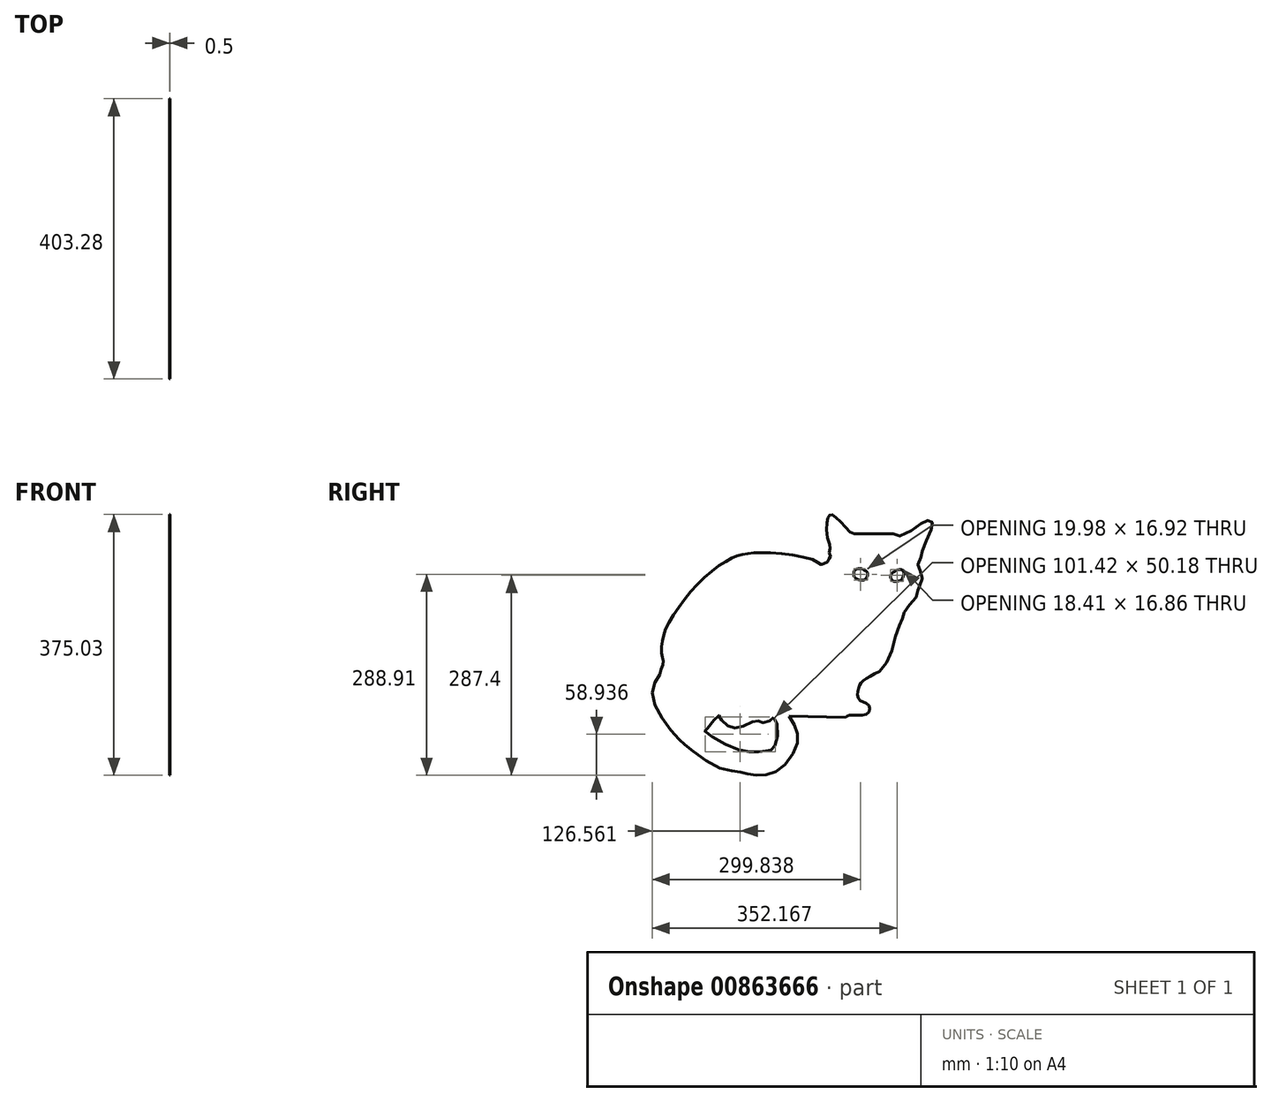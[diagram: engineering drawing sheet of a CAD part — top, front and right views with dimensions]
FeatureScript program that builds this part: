
annotation { "Feature Type Name" : "Feature", "Feature Type Description" : "" }
export const myFeature = defineFeature(function(context is Context, id is Id, definition is map)
    precondition{}
    {
        {
            var Q0;
            Q0=qCreatedBy(makeId("Right.planeOp"),FACE);
            var sketch = newSketch(context, id + "F0", { "sketchPlane" : qUnion([Q0])});
            skLineSegment(sketch, "E0", {"start": v(28.7, 28.02) * mm, "end": v(17.6, 28.02) * mm});
            skLineSegment(sketch, "E1", {"start": v(-11.4, 22.53) * mm, "end": v(-6.57, 22.53) * mm});
            skFitSpline(sketch, "E2", {"points": [v(17.6, 28.02) * mm, v(16.08, 28.8) * mm, v(13.76, 31.39) * mm, v(11.74, 33.19) * mm, v(11.02, 33.6) * mm, v(10.4, 33.43) * mm, v(9.92, 32.72) * mm, v(9.66, 31.07) * mm, v(9.8, 27.16) * mm, v(10.6, 24.27) * mm, v(10.44, 23.51) * mm, v(10.44, 22.03) * mm, v(10.73, 21.57) * mm, v(10.35, 21.16) * mm, v(10.15, 20.23) * mm, v(7.73, 19.24) * mm, v(6.81, 20.06) * mm, v(2, 21.54) * mm, v(-6.57, 22.53) * mm], "startDerivative": vector(-30.35, 0) * mm, "endDerivative": vector(-74.71, 0) * mm});
            skFitSpline(sketch, "E3", {"points": [v(-11.4, 22.53) * mm, v(-15.14, 21.98) * mm, v(-18.68, 20.56) * mm, v(-25.5, 15.58) * mm, v(-32.77, 7.2) * mm, v(-36.9, 0.27) * mm, v(-37.81, -3.74) * mm, v(-37.84, -7.26) * mm, v(-37.36, -8.84) * mm, v(-38.1, -10.96) * mm], "startDerivative": vector(-39.06, -4.14) * mm, "endDerivative": vector(-15.1, -29.61) * mm});
            skFitSpline(sketch, "E4", {"points": [v(-38.1, -10.96) * mm, v(-38.42, -12.24) * mm, v(-40.42, -16.1) * mm, v(-38.7, -23.58) * mm, v(-32.83, -31.2) * mm, v(-30.28, -33.4) * mm, v(-21.26, -39.4) * mm, v(-15.5, -40.47) * mm, v(-13, -41.14) * mm, v(-8.57, -41.34) * mm, v(-3.85, -39.6) * mm, v(0.92, -33.2) * mm, v(1.06, -28.86) * mm, v(-1.3, -24.34) * mm], "startDerivative": vector(-2.64, -30.16) * mm, "endDerivative": vector(-37.36, 60.1) * mm});
            skLineSegment(sketch, "E5", {"start": v(-1.3, -24.34) * mm, "end": v(15.03, -24.75) * mm});
            skFitSpline(sketch, "E6", {"points": [v(28.7, 28.02) * mm, v(30.43, 27.38) * mm, v(35.84, 30.4) * mm, v(38.13, 31.71) * mm, v(39.58, 31.9) * mm, v(40.06, 30.8) * mm, v(39, 27.67) * mm, v(37.12, 23) * mm, v(36.88, 21.74) * mm, v(35.92, 19.29) * mm, v(36.2, 18.23) * mm, v(37, 16.12) * mm, v(36.64, 13.46) * mm, v(35.72, 12.16) * mm, v(35.87, 11.68) * mm, v(35.1, 9.47) * mm, v(32.6, 6.62) * mm, v(31.57, 4.5) * mm, v(31.18, 3.07) * mm, v(29.78, 0) * mm, v(27.79, -7.29) * mm, v(24.75, -11.53) * mm], "startDerivative": vector(41.64, 0) * mm, "endDerivative": vector(-52.4, -48.6) * mm});
            skFitSpline(sketch, "E7", {"points": [v(15.03, -24.75) * mm, v(16.32, -24.16) * mm, v(21.26, -23.75) * mm, v(21.54, -21.12) * mm, v(18.87, -19.58) * mm, v(18.75, -16.42) * mm, v(19.8, -14.52) * mm, v(24.75, -11.53) * mm], "startDerivative": vector(9.62, 8.2) * mm, "endDerivative": vector(30.76, 16.11) * mm});
            skFitSpline(sketch, "E8", {"points": [v(-5.64, -24.8) * mm, v(-4.48, -29.98) * mm, v(-6.18, -34) * mm, v(-7.4, -34.34) * mm, v(-10.75, -34.75) * mm, v(-18.03, -33.2) * mm, v(-25.52, -28.62) * mm, v(-24.98, -28.08) * mm, v(-21.64, -24.26) * mm, v(-21.23, -24.74) * mm, v(-18.78, -27.26) * mm, v(-15.3, -27.6) * mm, v(-10.54, -25.7) * mm, v(-9.59, -26.1) * mm, v(-7.14, -26.03) * mm, v(-5.64, -24.8) * mm]});
            skFitSpline(sketch, "E9", {"points": [v(17.37, 16.83) * mm, v(17.57, 17.38) * mm, v(19.06, 18.07) * mm, v(20.64, 17.46) * mm, v(21.35, 16.83) * mm, v(21.2, 15.58) * mm, v(19.8, 14.66) * mm, v(17.83, 15.35) * mm], "startDerivative": vector(0.7, 5.6) * mm, "endDerivative": vector(-8.53, 8) * mm});
            skFitSpline(sketch, "E10", {"points": [v(17.83, 15.35) * mm, v(17.37, 16) * mm], "startDerivative": vector(-0.46, 0.37) * mm, "endDerivative": vector(-0.17, 0.77) * mm});
            skFitSpline(sketch, "E11", {"points": [v(17.37, 16) * mm, v(17.37, 16.83) * mm], "startDerivative": vector(0, 0.83) * mm, "endDerivative": vector(0, 0.83) * mm});
            skFitSpline(sketch, "E12", {"points": [v(28, 15.43) * mm, v(28.82, 14.43) * mm, v(30.63, 14.57) * mm, v(31.54, 15.49) * mm, v(31.66, 17.3) * mm, v(30.2, 17.75) * mm, v(29.05, 17.15) * mm, v(28.45, 16.72) * mm, v(28, 16) * mm, v(28, 15.43) * mm]});
            skSolve(sketch);
        }
        {
            var Q0;
            Q0 = qSketchRegion(id + "F0", true);
            extrude(context, id + "F1", {"entities" : qUnion([Q0]), "depth" : .1 * mm, "offsetDistance" : 25.4 * mm});
        }
        {
            var Q0;
            Q0=makeQuery(id+"F1.opExtrude","SWEPT_BODY",BODY,{"disambiguationData":[OSD([sQuery(id+"F0.wireOp",EDGE,"E0"),sQuery(id+"F0.wireOp",EDGE,"E1"),sQuery(id+"F0.wireOp",EDGE,"E2"),sQuery(id+"F0.wireOp",EDGE,"E3"),sQuery(id+"F0.wireOp",EDGE,"E4"),sQuery(id+"F0.wireOp",EDGE,"E5"),sQuery(id+"F0.wireOp",EDGE,"E6"),sQuery(id+"F0.wireOp",EDGE,"E7"),sQuery(id+"F0.wireOp",EDGE,"E8"),sQuery(id+"F0.wireOp",EDGE,"E9"),sQuery(id+"F0.wireOp",EDGE,"E10"),sQuery(id+"F0.wireOp",EDGE,"E11"),sQuery(id+"F0.wireOp",EDGE,"E12")])]});
            var Q1;
            Q1=qCreatedBy(makeId("Origin.pointOp"),VERTEX);
            transform(context, id + "F2", {"entities" : qUnion([Q0]), "transformType" : TransformType.SCALE_UNIFORMLY, "scale" : 5, "scalePoint" : qUnion([Q1]), "makeCopy" : false});
        }
    });
